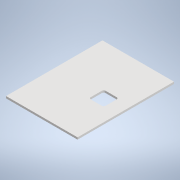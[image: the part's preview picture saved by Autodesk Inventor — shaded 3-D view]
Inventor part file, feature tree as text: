
AUTODESK INVENTOR PART (.ipt)
format: ipt  version: 2020 (Build 240168000, 168)  size: 109,056 bytes
history: native  units: in
note: dims shown in document units (in); Inventor stores cm internally (conversion verified against a paired STEP export)
features: other x3, extrude x2, sketch x2, reference x1
ambient origin geometry x8: Origin, YZ Plane, XZ Plane, XY Plane, X Axis, Y Axis, Z Axis, Center Point
bodies: Solid1 (feature_tree)
feature tree (8):
  extrude  "Extrusion1"  Depth=2.4409in
  extrude  "Extrusion2"  Depth=0.3937in TaperAngle=0.0deg
  sketch  "Sketch1"  dims[d0=3.8319in d1=2.4409in]
  sketch  "Sketch2"  dims[d2=0.0787in d3=0.0in d4=0.3937in d5=0.0in]
  reference  "Reference1"
  other  "<userpath>\Downloads\R2D2_-_Servo_Driven_Hinge_Design\r2d2\Assembly.iam"
  other  "Assembly.iam"
  other  "horn_base:1"
